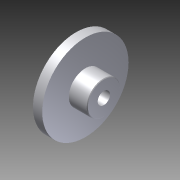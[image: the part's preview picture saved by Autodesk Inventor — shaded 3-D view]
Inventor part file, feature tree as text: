
AUTODESK INVENTOR PART (.ipt)
format: ipt  version: 2012 (Build 160160000, 160)  size: 602,112 bytes
history: native  units: in
note: dims shown in document units (in); Inventor stores cm internally (conversion verified against a paired STEP export)
features: extrude x2, sketch x1, imported_body x1
ambient origin geometry x8: Origin, YZ Plane, XZ Plane, XY Plane, X Axis, Y Axis, Z Axis, Center Point
feature tree (4):
  sketch  "Sketch1"  dims[d0=0.25in d1=0.5625in d2=0.0in d3=1.75in d4=1.0in d5=0.0in]
  extrude  "Extrusion1"  Depth=0.5625in TaperAngle=0.0deg
  extrude  "Extrusion2"  Depth=1.75in
  imported_body  "Base1"
